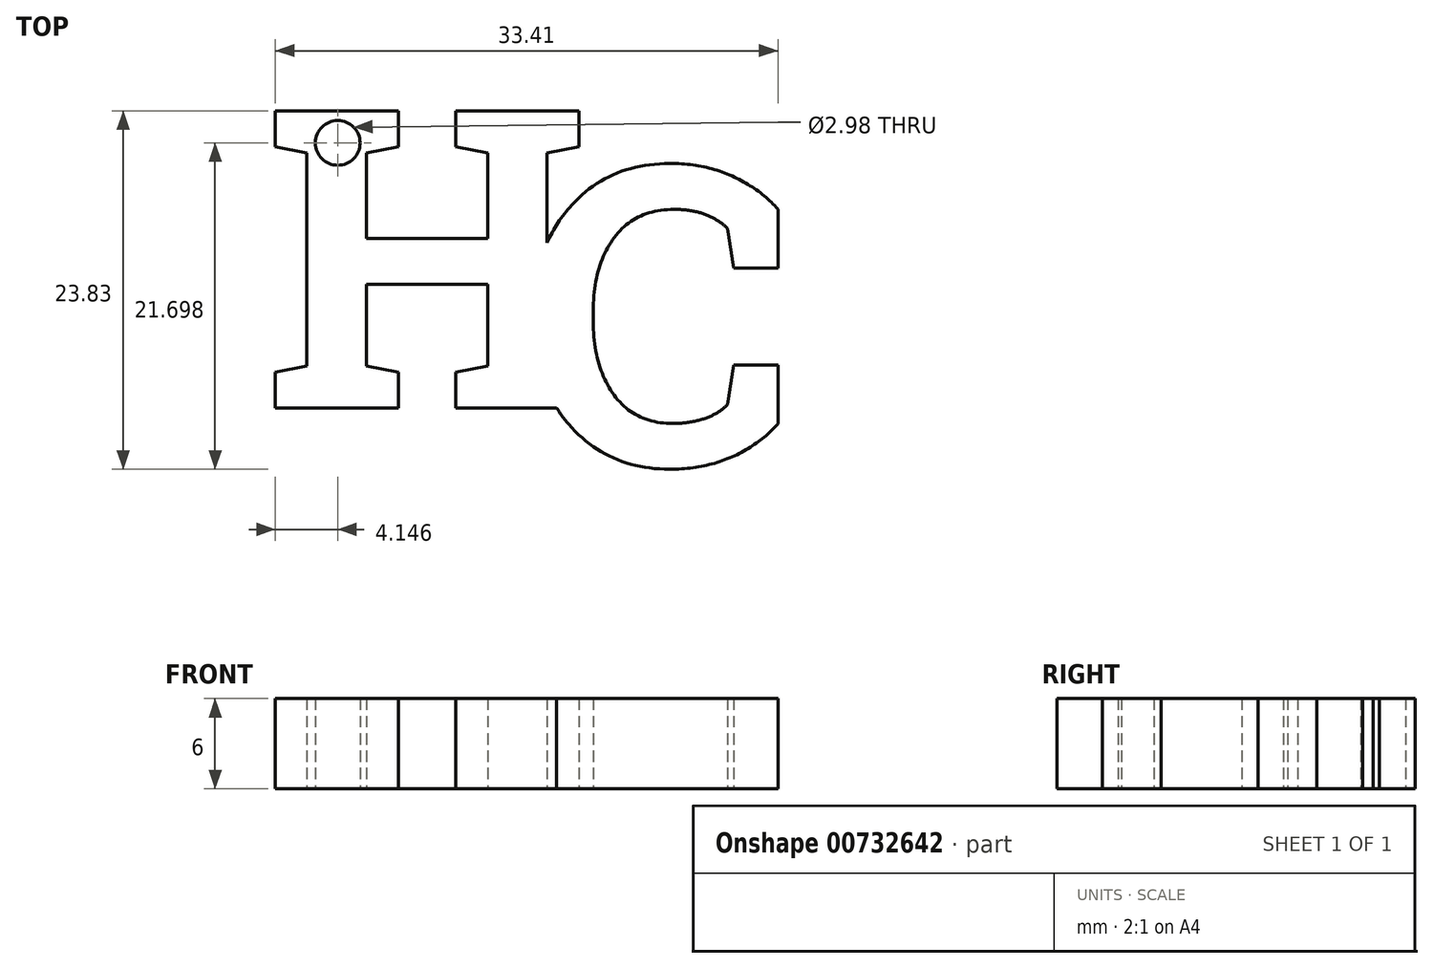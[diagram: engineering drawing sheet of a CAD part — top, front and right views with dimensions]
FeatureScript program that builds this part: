
annotation { "Feature Type Name" : "Feature", "Feature Type Description" : "" }
export const myFeature = defineFeature(function(context is Context, id is Id, definition is map)
    precondition{}
    {
        {
            var Q0;
            Q0=qCreatedBy(makeId("Top.planeOp"),FACE);
            var sketch = newSketch(context, id + "F0", { "sketchPlane" : qUnion([Q0])});
            skText(sketch, "E0", { "text": "H", "fontName": "RobotoSlab-Bold.ttf"});
            skText(sketch, "E1", { "text": "C", "fontName": "RobotoSlab-Bold.ttf"});
            const initialGuessF0  = {"E0": [-0.04744, 0.01906, 1, 0, 0.02], "E1": [-0.03021, 0.01527, 1, 0, 0.02]};
            skSetInitialGuess(sketch, initialGuessF0);
            skSolve(sketch);
        }
        {
            var Q0;
            Q0 = qSketchRegion(id + "F0", true);
            extrude(context, id + "F1", {"entities" : qUnion([Q0]), "depth" : 6 * mm, "offsetDistance" : 25 * mm});
        }
        {
            var Q0;
            Q0=qCreatedBy(makeId("Top.planeOp"),FACE);
            var sketch = newSketch(context, id + "F2", { "sketchPlane" : qUnion([Q0])});
            skCircle(sketch, "E2", {"center": v(-42.53, 36.68) * mm, "radius": 1.49 * mm});
            skSolve(sketch);
        }
        {
            var Q0;
            Q0 = qSketchRegion(id + "F2", true);
            extrude(context, id + "F3", {"entities" : qUnion([Q0]), "operationType" : NewBodyOperationType.REMOVE, "depth" : 6 * mm, "offsetDistance" : 25 * mm});
        }
    });
